# Revit family: Suszarka_do_rak_PASSAT V
name_source: partatom
category: Wyposażenie elektryczne
units: mm (PartAtom-declared; Revit-internal decimal feet)

## family parameters
Konfiguracja rozdzielnicy = Dwie kolumny, obwody w poprzek
Obiekt nadrzędny = Ściana
Punkt obliczania pomieszczeń = Nie
Tnij formami wycięć po wczytaniu = Nie
Typ części = Rozdzielnica
Współdzielony = Nie
Wymiar okrągłego złącza = Użyj średnicy
Zawsze pionowo = Tak

## types (2) — shared parameters
Depth / Glebokosc = 150 mm  [stored 0.492126 ft]
Height / Wysokosc = 255 mm  [stored 0.836614 ft]
Manufacturer code / Kod producenta = 5901764293972
Material = plastic ABS, biały
Material finish / Wykonczenie = Stal nierdzewna 304 szczotkowana, mat
Model = PASSAT V
Napięcie = 1350
Opis = Suszarka do rąk 1350 Passat V to solidne, nowoczesne i trwałe urządzenie, będące niezawodnym elementem łazienki ogólnodostępnej. Jest to suszarka automatyczna- jej włączenie następuje po wsunięciu rąk w pole działania fotokomórki. Suszarka do rąk Passat wykonana jest ze stali nierdzewnej matowej. Urządzenie posiada specjalną dyszę, która zapewnia krótki czas suszenia oraz skuteczność suszarki. Passat łączy w sobie najważniejsze cechy suszarek do rąk: bardzo wysoką wydajność oraz ekonomiczny pobór mocy. Zaspokaja on oczekiwania nawet najbardziej wymagających użytkowników.
Producent = FANECO.com
Product code / Kod produktu = D1350SCB
URL = https://faneco.com
Weight / Waga = 3 kg
Width / Szerokosc = 173 mm  [stored 0.567585 ft]

## type names (no varying parameters)
- D1350SCB
- Type 1

note: [stored X ft] marks values corroborated as IEEE doubles in the binary element streams (Revit-internal decimal feet)

## geometry (parser evidence)
native form markers: Blend x10, Sweep x6
no freeform markers — native parametric forms only
